# Revit family: DockLeveler_H-Series_BlueGiant
name_source: partatom
category: Specialty Equipment
units: mm (PartAtom-declared; Revit-internal decimal feet)

## family parameters
Cut with Voids When Loaded = No
Enable Cutting in Views = No
Host = Face
Maintain Annotation Orientation = No
Part Type = Normal
Room Calculation Point = No
Round Connector Dimension = Use Diameter
Shared = No

## types (15) — shared parameters
Assembly Code = E1030300
Available Options = as Specified
Capacity = [30000][35000][40000][45000][50000][60000][80000] lbs
Construction Details = http://www.arcat.com
Green Building-LEED = http://www.arcat.com
Installation-Fabrication = http://www.bluegiant.com
Keynote = 11600
Manufacturer = Blue Giant Equipment Corp.
Manufacturer Fax = 905-457-2313
Manufacturer Website = http://www.bluegiant.com
Pit Depth = 20 "
Product Data = http://www.arcat.com
Rear Pit Offset = 0.5 "
Revision = R1_06_2014
Sales Information = http://www.bluegiant.com
Send Message = http://www.arcat.com
SpecWizard = http://www.arcat.com
Specification = http://www.arcat.com
URL = http://www.bluegiant.com
zero-valued in all types: Default Elevation, Expected Lifespan (Years), Lip Inset, Maintenance Schedule (Months), Warranty Duration (Years)

## per-type parameters (varying)
| type | Description | Pit Length | Pit Width | Unit Width |
| 7014 | Blue Giant HA7014 Hydraulic Dock Leveler as Specified | 159 " | 80 " | 83 " |
| 7012 | Blue Giant HA7012 Hydraulic Dock Leveler as Specified | 135 " | 85 " | 83 " |
| 7010 | Blue Giant HA7010 Hydraulic Dock Leveler as Specified | 111 " | 85 " | 83 " |
| 7008 | Blue Giant HA7008 Hydraulic Dock Leveler as Specified | 87 " | 85 " | 83 " |
| 7006 | Blue Giant HA7006 Hydraulic Dock Leveler as Specified | 63 " | 85 " | 83 " |
| 6614 | Blue Giant HA6614 Hydraulic Dock Leveler as Specified | 159 " | 80 " | 78 " |
| 6612 | Blue Giant HA6612 Hydraulic Dock Leveler as Specified | 135 " | 80 " | 78 " |
| 6610 | Blue Giant HA6610 Hydraulic Dock Leveler as Specified | 111 " | 80 " | 78 " |
| 6608 | Blue Giant HA6608 Hydraulic Dock Leveler as Specified | 87 " | 80 " | 78 " |
| 6606 | Blue Giant HA6606 Hydraulic Dock Leveler as Specified | 63 " | 80 " | 78 " |
| 6014 | Blue Giant HA6014 Hydraulic Dock Leveler as Specified | 159 " | 74 " | 72 " |
| 6012 | Blue Giant HA6012 Hydraulic Dock Leveler as Specified | 135 " | 74 " | 72 " |
| 6010 | Blue Giant HA6010 Hydraulic Dock Leveler as Specified | 111 " | 74 " | 72 " |
| 6008 | Blue Giant HA6008 Hydraulic Dock Leveler as Specified | 87 " | 74 " | 72 " |
| 6006 | Blue Giant HA6006 Hydraulic Dock Leveler as Specified | 63 " | 74 " | 72 " |

note: column(s) folded — value = type name in every type: Model

## geometry (parser evidence)
native form markers: Blend x8, Sweep x3
no freeform markers — native parametric forms only
